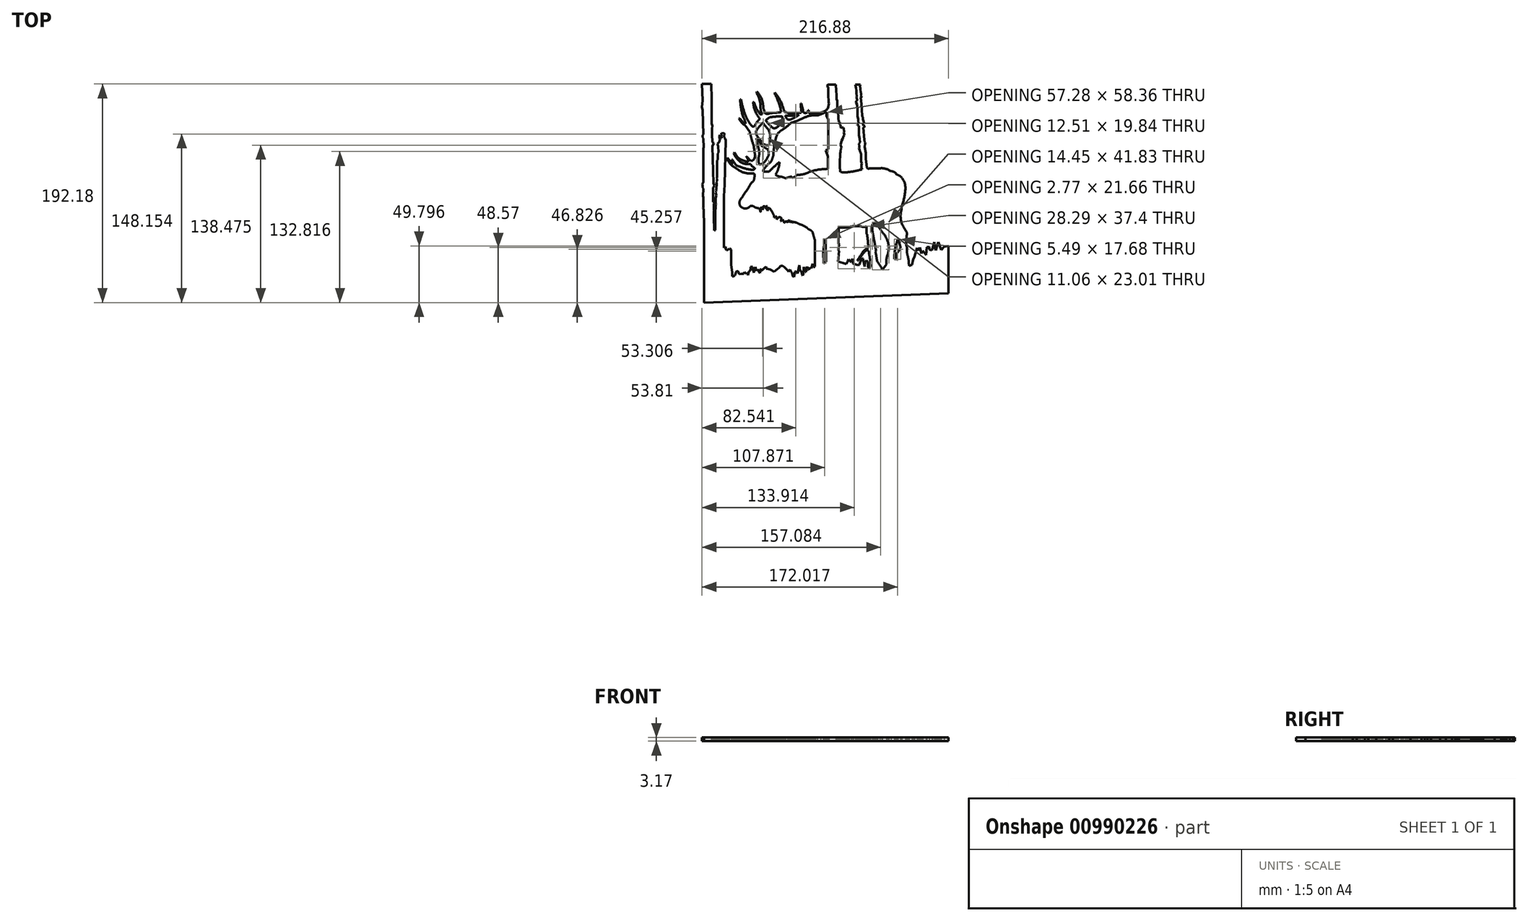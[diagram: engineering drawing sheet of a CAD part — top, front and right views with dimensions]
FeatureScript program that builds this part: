
annotation { "Feature Type Name" : "Feature", "Feature Type Description" : "" }
export const myFeature = defineFeature(function(context is Context, id is Id, definition is map)
    precondition{}
    {
        {
            var Q0;
            Q0=qCreatedBy(makeId("Top.planeOp"),FACE);
            var sketch = newSketch(context, id + "F0", { "sketchPlane" : qUnion([Q0])});
            skArc(sketch, "E0", {"start": v(289.3, 112.58) * mm, "mid": v(291.23, 120.3) * mm, "end": v(292.3, 128.2) * mm});
            skArc(sketch, "E1", {"start": v(292.3, 128.2) * mm, "mid": v(291.34, 133.48) * mm, "end": v(288.53, 138.04) * mm});
            skArc(sketch, "E2", {"start": v(288.53, 138.04) * mm, "mid": v(286.45, 139.47) * mm, "end": v(284.11, 140.41) * mm});
            skArc(sketch, "E3", {"start": v(284.11, 140.41) * mm, "mid": v(282.3, 142.56) * mm, "end": v(279.5, 142.88) * mm});
            skArc(sketch, "E4", {"start": v(279.5, 142.88) * mm, "mid": v(274.89, 145.26) * mm, "end": v(269.71, 145.75) * mm});
            skArc(sketch, "E5", {"start": v(269.71, 145.75) * mm, "mid": v(260.83, 145.51) * mm, "end": v(252.03, 144.24) * mm});
            skArc(sketch, "E6", {"start": v(239.59, 142.06) * mm, "mid": v(245.85, 142.93) * mm, "end": v(252.03, 144.24) * mm});
            skArc(sketch, "E7", {"start": v(231.89, 143.51) * mm, "mid": v(235.66, 142.4) * mm, "end": v(239.59, 142.06) * mm});
            skArc(sketch, "E8", {"start": v(231.89, 143.51) * mm, "mid": v(226.66, 145.01) * mm, "end": v(221.22, 144.97) * mm});
            skArc(sketch, "E9", {"start": v(221.22, 144.97) * mm, "mid": v(212.73, 143.94) * mm, "end": v(204.68, 141.05) * mm});
            skArc(sketch, "E10", {"start": v(196.66, 139.78) * mm, "mid": v(200.7, 140.17) * mm, "end": v(204.68, 141.05) * mm});
            skArc(sketch, "E11", {"start": v(193.06, 137.4) * mm, "mid": v(195.05, 138.3) * mm, "end": v(196.66, 139.78) * mm});
            skArc(sketch, "E12", {"start": v(192.24, 138.4) * mm, "mid": v(192.5, 137.79) * mm, "end": v(193.06, 137.4) * mm});
            skArc(sketch, "E13", {"start": v(192.24, 138.4) * mm, "mid": v(189.53, 137.79) * mm, "end": v(186.88, 136.94) * mm});
            skArc(sketch, "E14", {"start": v(186.88, 136.94) * mm, "mid": v(184.76, 137.84) * mm, "end": v(182.54, 138.4) * mm});
            skArc(sketch, "E15", {"start": v(178.04, 140.2) * mm, "mid": v(180.12, 138.87) * mm, "end": v(182.54, 138.4) * mm});
            skArc(sketch, "E16", {"start": v(178.04, 140.2) * mm, "mid": v(179.67, 143.2) * mm, "end": v(180.75, 146.46) * mm});
            skArc(sketch, "E17", {"start": v(180.75, 146.46) * mm, "mid": v(181.29, 148.76) * mm, "end": v(181.48, 151.1) * mm});
            skArc(sketch, "E18", {"start": v(181.48, 151.1) * mm, "mid": v(176.84, 147.09) * mm, "end": v(172.37, 142.88) * mm});
            skArc(sketch, "E19", {"start": v(172.37, 142.88) * mm, "mid": v(169.86, 142.9) * mm, "end": v(167.36, 142.63) * mm});
            skArc(sketch, "E20", {"start": v(167.36, 144.13) * mm, "mid": v(167.22, 143.38) * mm, "end": v(167.36, 142.63) * mm});
            skArc(sketch, "E21", {"start": v(172.84, 150.42) * mm, "mid": v(169.85, 147.49) * mm, "end": v(167.36, 144.13) * mm});
            skArc(sketch, "E22", {"start": v(172.84, 150.42) * mm, "mid": v(174.3, 152.06) * mm, "end": v(175.16, 154.07) * mm});
            skArc(sketch, "E23", {"start": v(175.16, 154.07) * mm, "mid": v(175.98, 156.69) * mm, "end": v(176.22, 159.42) * mm});
            skArc(sketch, "E24", {"start": v(176.22, 159.42) * mm, "mid": v(176.58, 162.71) * mm, "end": v(176.58, 166.02) * mm});
            skArc(sketch, "E25", {"start": v(179.42, 175.5) * mm, "mid": v(177.9, 170.79) * mm, "end": v(176.58, 166.02) * mm});
            skArc(sketch, "E26", {"start": v(183.87, 179.43) * mm, "mid": v(181.42, 177.71) * mm, "end": v(179.42, 175.5) * mm});
            skArc(sketch, "E27", {"start": v(183.87, 179.43) * mm, "mid": v(187.89, 182.31) * mm, "end": v(191.59, 185.6) * mm});
            skArc(sketch, "E28", {"start": v(191.59, 185.6) * mm, "mid": v(197.29, 187.56) * mm, "end": v(202.79, 190.02) * mm});
            skArc(sketch, "E29", {"start": v(213.12, 192.38) * mm, "mid": v(207.8, 191.86) * mm, "end": v(202.79, 190.02) * mm});
            skArc(sketch, "E30", {"start": v(213.12, 192.38) * mm, "mid": v(215.42, 192.38) * mm, "end": v(217.57, 193.18) * mm});
            skArc(sketch, "E31", {"start": v(217.57, 193.18) * mm, "mid": v(220.8, 194.41) * mm, "end": v(223.92, 195.9) * mm});
            skArc(sketch, "E32", {"start": v(223.92, 195.9) * mm, "mid": v(223.09, 196.45) * mm, "end": v(222.1, 196.3) * mm});
            skArc(sketch, "E33", {"start": v(214.93, 194.33) * mm, "mid": v(218.63, 194.92) * mm, "end": v(222.1, 196.3) * mm});
            skArc(sketch, "E34", {"start": v(209.07, 193.78) * mm, "mid": v(212, 194.03) * mm, "end": v(214.93, 194.33) * mm});
            skArc(sketch, "E35", {"start": v(207.58, 194.33) * mm, "mid": v(208.28, 193.93) * mm, "end": v(209.07, 193.78) * mm});
            skArc(sketch, "E36", {"start": v(207.24, 196.65) * mm, "mid": v(207.27, 195.47) * mm, "end": v(207.58, 194.33) * mm});
            skArc(sketch, "E37", {"start": v(205.66, 194.61) * mm, "mid": v(206.33, 195.56) * mm, "end": v(206.7, 196.65) * mm});
            skArc(sketch, "E38", {"start": v(202.79, 194.61) * mm, "mid": v(204.22, 194.36) * mm, "end": v(205.66, 194.61) * mm});
            skArc(sketch, "E39", {"start": v(202.01, 197.08) * mm, "mid": v(202.26, 195.8) * mm, "end": v(202.79, 194.61) * mm});
            skLineSegment(sketch, "E40", {"start": v(202.01, 197.08) * mm, "end": v(200.49, 202.8) * mm});
            skLineSegment(sketch, "E41", {"start": v(200.49, 202.8) * mm, "end": v(200.22, 202.73) * mm});
            skLineSegment(sketch, "E42", {"start": v(200.22, 202.73) * mm, "end": v(200.49, 194.54) * mm});
            skArc(sketch, "E43", {"start": v(193.33, 189.62) * mm, "mid": v(197.21, 191.64) * mm, "end": v(200.49, 194.54) * mm});
            skArc(sketch, "E44", {"start": v(188.45, 188.76) * mm, "mid": v(190.99, 188.63) * mm, "end": v(193.33, 189.62) * mm});
            skArc(sketch, "E45", {"start": v(186.3, 193.22) * mm, "mid": v(187.09, 190.85) * mm, "end": v(188.45, 188.76) * mm});
            skArc(sketch, "E46", {"start": v(186.3, 193.22) * mm, "mid": v(185.25, 197.3) * mm, "end": v(183.9, 201.29) * mm});
            skArc(sketch, "E47", {"start": v(183.9, 201.29) * mm, "mid": v(181.14, 207.1) * mm, "end": v(177.37, 212.32) * mm});
            skArc(sketch, "E48", {"start": v(183.07, 195.14) * mm, "mid": v(180.76, 203.46) * mm, "end": v(177.37, 211.4) * mm});
            skArc(sketch, "E49", {"start": v(183.9, 186.66) * mm, "mid": v(183.95, 190.94) * mm, "end": v(183.07, 195.14) * mm});
            skArc(sketch, "E50", {"start": v(177.97, 181.1) * mm, "mid": v(181.36, 183.42) * mm, "end": v(183.9, 186.66) * mm});
            skArc(sketch, "E51", {"start": v(175, 181.65) * mm, "mid": v(176.4, 180.96) * mm, "end": v(177.97, 181.1) * mm});
            skArc(sketch, "E52", {"start": v(166.84, 190.72) * mm, "mid": v(170.75, 186.04) * mm, "end": v(175, 181.65) * mm});
            skArc(sketch, "E53", {"start": v(161.16, 198.35) * mm, "mid": v(163.8, 194.38) * mm, "end": v(166.84, 190.72) * mm});
            skArc(sketch, "E54", {"start": v(158.99, 204.03) * mm, "mid": v(160.06, 201.19) * mm, "end": v(161.16, 198.35) * mm});
            skArc(sketch, "E55", {"start": v(158.3, 203.88) * mm, "mid": v(159.92, 196.73) * mm, "end": v(163.4, 190.28) * mm});
            skArc(sketch, "E56", {"start": v(163.4, 190.28) * mm, "mid": v(167.42, 184.97) * mm, "end": v(171.65, 179.83) * mm});
            skArc(sketch, "E57", {"start": v(173.38, 173.07) * mm, "mid": v(172.95, 176.56) * mm, "end": v(171.65, 179.83) * mm});
            skArc(sketch, "E58", {"start": v(172.4, 166.8) * mm, "mid": v(173.1, 169.9) * mm, "end": v(173.38, 173.07) * mm});
            skArc(sketch, "E59", {"start": v(169.11, 166.37) * mm, "mid": v(170.85, 165.89) * mm, "end": v(172.4, 166.8) * mm});
            skArc(sketch, "E60", {"start": v(166.33, 168.16) * mm, "mid": v(167.52, 166.95) * mm, "end": v(169.11, 166.37) * mm});
            skArc(sketch, "E61", {"start": v(166.33, 168.16) * mm, "mid": v(165.47, 169.7) * mm, "end": v(164.25, 170.99) * mm});
            skArc(sketch, "E62", {"start": v(161.16, 175.18) * mm, "mid": v(162.63, 173.03) * mm, "end": v(164.25, 170.99) * mm});
            skArc(sketch, "E63", {"start": v(161.16, 178.97) * mm, "mid": v(160.88, 177.07) * mm, "end": v(161.16, 175.18) * mm});
            skArc(sketch, "E64", {"start": v(166.84, 185.72) * mm, "mid": v(163.84, 182.48) * mm, "end": v(161.16, 178.97) * mm});
            skArc(sketch, "E65", {"start": v(164.25, 189.12) * mm, "mid": v(161.66, 186.2) * mm, "end": v(159.52, 182.94) * mm});
            skArc(sketch, "E66", {"start": v(157.26, 182.66) * mm, "mid": v(158.44, 182.4) * mm, "end": v(159.52, 182.94) * mm});
            skArc(sketch, "E67", {"start": v(153.07, 189.08) * mm, "mid": v(155, 185.77) * mm, "end": v(157.26, 182.66) * mm});
            skArc(sketch, "E68", {"start": v(151, 193.71) * mm, "mid": v(152, 191.38) * mm, "end": v(153.07, 189.08) * mm});
            skArc(sketch, "E69", {"start": v(147.59, 206.44) * mm, "mid": v(149.02, 200) * mm, "end": v(151, 193.71) * mm});
            skArc(sketch, "E70", {"start": v(147.04, 206.44) * mm, "mid": v(147.73, 198.23) * mm, "end": v(149.9, 190.28) * mm});
            skArc(sketch, "E71", {"start": v(151.64, 185.2) * mm, "mid": v(151, 187.82) * mm, "end": v(149.9, 190.28) * mm});
            skArc(sketch, "E72", {"start": v(150.85, 185.2) * mm, "mid": v(151.25, 185.08) * mm, "end": v(151.64, 185.2) * mm});
            skArc(sketch, "E73", {"start": v(146.46, 189.67) * mm, "mid": v(148.46, 187.25) * mm, "end": v(150.85, 185.2) * mm});
            skArc(sketch, "E74", {"start": v(146.06, 189.42) * mm, "mid": v(148.1, 186.08) * mm, "end": v(151.15, 183.65) * mm});
            skArc(sketch, "E75", {"start": v(152.05, 182.27) * mm, "mid": v(151.61, 182.97) * mm, "end": v(151.15, 183.65) * mm});
            skArc(sketch, "E76", {"start": v(155.29, 177.66) * mm, "mid": v(153.75, 180.02) * mm, "end": v(152.05, 182.27) * mm});
            skArc(sketch, "E77", {"start": v(157.02, 170.79) * mm, "mid": v(156.22, 174.24) * mm, "end": v(155.29, 177.66) * mm});
            skArc(sketch, "E78", {"start": v(159.52, 160.12) * mm, "mid": v(158.72, 165.56) * mm, "end": v(157.02, 170.79) * mm});
            skArc(sketch, "E79", {"start": v(159.29, 153.94) * mm, "mid": v(159.9, 157.01) * mm, "end": v(159.52, 160.12) * mm});
            skArc(sketch, "E80", {"start": v(156.55, 152.14) * mm, "mid": v(158.13, 152.72) * mm, "end": v(159.29, 153.94) * mm});
            skArc(sketch, "E81", {"start": v(153.07, 155.64) * mm, "mid": v(154.73, 153.8) * mm, "end": v(156.55, 152.14) * mm});
            skArc(sketch, "E82", {"start": v(154.42, 152.35) * mm, "mid": v(153.37, 154.26) * mm, "end": v(152.25, 156.11) * mm});
            skArc(sketch, "E83", {"start": v(153.07, 151.65) * mm, "mid": v(153.84, 151.81) * mm, "end": v(154.42, 152.35) * mm});
            skArc(sketch, "E84", {"start": v(141.96, 159.64) * mm, "mid": v(146.43, 154.14) * mm, "end": v(153.07, 151.65) * mm});
            skArc(sketch, "E85", {"start": v(141.29, 159.06) * mm, "mid": v(144.26, 153.94) * mm, "end": v(148.97, 150.36) * mm});
            skArc(sketch, "E86", {"start": v(148.97, 150.36) * mm, "mid": v(152.47, 149.42) * mm, "end": v(156.1, 149.39) * mm});
            skArc(sketch, "E87", {"start": v(156.1, 149.39) * mm, "mid": v(157.72, 147.28) * mm, "end": v(160, 145.93) * mm});
            skArc(sketch, "E88", {"start": v(158.4, 144.31) * mm, "mid": v(159.39, 144.94) * mm, "end": v(160, 145.93) * mm});
            skArc(sketch, "E89", {"start": v(148.12, 146.55) * mm, "mid": v(153.17, 145) * mm, "end": v(158.4, 144.31) * mm});
            skArc(sketch, "E90", {"start": v(148.12, 146.55) * mm, "mid": v(146.4, 147.2) * mm, "end": v(144.6, 147.58) * mm});
            skArc(sketch, "E91", {"start": v(140.2, 153.4) * mm, "mid": v(142.03, 150.21) * mm, "end": v(144.6, 147.58) * mm});
            skArc(sketch, "E92", {"start": v(139.58, 153.27) * mm, "mid": v(139.92, 151.55) * mm, "end": v(140.69, 149.97) * mm});
            skArc(sketch, "E93", {"start": v(139.76, 150.36) * mm, "mid": v(140.17, 150.04) * mm, "end": v(140.69, 149.97) * mm});
            skArc(sketch, "E94", {"start": v(135.7, 155.25) * mm, "mid": v(137.53, 152.63) * mm, "end": v(139.76, 150.36) * mm});
            skArc(sketch, "E95", {"start": v(135.5, 154.22) * mm, "mid": v(137.59, 150.22) * mm, "end": v(141, 147.27) * mm});
            skArc(sketch, "E96", {"start": v(141, 147.27) * mm, "mid": v(144.17, 145.11) * mm, "end": v(147.43, 143.1) * mm});
            skArc(sketch, "E97", {"start": v(147.43, 143.1) * mm, "mid": v(152.5, 141.42) * mm, "end": v(157.84, 141.17) * mm});
            skArc(sketch, "E98", {"start": v(159.67, 140.41) * mm, "mid": v(158.87, 141.07) * mm, "end": v(157.84, 141.17) * mm});
            skArc(sketch, "E99", {"start": v(158.7, 134.3) * mm, "mid": v(159.38, 137.33) * mm, "end": v(159.67, 140.41) * mm});
            skArc(sketch, "E100", {"start": v(158.7, 134.3) * mm, "mid": v(156.39, 132.34) * mm, "end": v(154.95, 129.66) * mm});
            skArc(sketch, "E101", {"start": v(150.6, 123.43) * mm, "mid": v(152.87, 126.48) * mm, "end": v(154.95, 129.66) * mm});
            skArc(sketch, "E102", {"start": v(150.6, 123.43) * mm, "mid": v(149.9, 122.39) * mm, "end": v(149.4, 121.22) * mm});
            skArc(sketch, "E103", {"start": v(149.4, 121.22) * mm, "mid": v(147.98, 119.38) * mm, "end": v(146.62, 117.49) * mm});
            skArc(sketch, "E104", {"start": v(146.62, 117.49) * mm, "mid": v(146.32, 115.01) * mm, "end": v(146.85, 112.58) * mm});
            skArc(sketch, "E105", {"start": v(146.85, 112.58) * mm, "mid": v(149.45, 110.75) * mm, "end": v(152.62, 110.54) * mm});
            skArc(sketch, "E106", {"start": v(152.62, 110.54) * mm, "mid": v(154.4, 111.28) * mm, "end": v(155.84, 112.58) * mm});
            skArc(sketch, "E107", {"start": v(158.7, 112.26) * mm, "mid": v(157.3, 112.65) * mm, "end": v(155.84, 112.58) * mm});
            skArc(sketch, "E108", {"start": v(158.7, 112.26) * mm, "mid": v(160.93, 111.06) * mm, "end": v(163.4, 110.54) * mm});
            skArc(sketch, "E109", {"start": v(165.3, 192.45) * mm, "mid": v(165.71, 193.54) * mm, "end": v(165.55, 194.68) * mm});
            skArc(sketch, "E110", {"start": v(164.7, 201.29) * mm, "mid": v(164.88, 197.95) * mm, "end": v(165.55, 194.68) * mm});
            skArc(sketch, "E111", {"start": v(164.7, 201.29) * mm, "mid": v(164.52, 203.46) * mm, "end": v(163.96, 205.57) * mm});
            skArc(sketch, "E112", {"start": v(163.96, 205.57) * mm, "mid": v(162.94, 208.94) * mm, "end": v(161.16, 211.98) * mm});
            skArc(sketch, "E113", {"start": v(166.33, 205.57) * mm, "mid": v(164.38, 209.58) * mm, "end": v(161.64, 213.1) * mm});
            skArc(sketch, "E114", {"start": v(167.3, 198.35) * mm, "mid": v(167, 201.99) * mm, "end": v(166.33, 205.57) * mm});
            skArc(sketch, "E115", {"start": v(168.81, 194.23) * mm, "mid": v(168.12, 196.32) * mm, "end": v(167.3, 198.35) * mm});
            skArc(sketch, "E116", {"start": v(168.81, 194.23) * mm, "mid": v(170.96, 193.47) * mm, "end": v(173.12, 194.23) * mm});
            skArc(sketch, "E117", {"start": v(173.12, 194.23) * mm, "mid": v(178.1, 194.59) * mm, "end": v(183.07, 195.14) * mm});
            skArc(sketch, "E118", {"start": v(173.62, 190.72) * mm, "mid": v(171.28, 189.46) * mm, "end": v(169.32, 187.68) * mm});
            skArc(sketch, "E119", {"start": v(183.9, 191.5) * mm, "mid": v(178.75, 191.21) * mm, "end": v(173.62, 190.72) * mm});
            skArc(sketch, "E120", {"start": v(189.3, 194.23) * mm, "mid": v(187.65, 194.94) * mm, "end": v(185.85, 195.14) * mm});
            skArc(sketch, "E121", {"start": v(193.24, 191.98) * mm, "mid": v(189.96, 191.93) * mm, "end": v(186.67, 191.86) * mm});
            skArc(sketch, "E122", {"start": v(198.82, 192.88) * mm, "mid": v(196, 192.6) * mm, "end": v(193.24, 191.98) * mm});
            skArc(sketch, "E123", {"start": v(192.07, 194.23) * mm, "mid": v(196.28, 194.3) * mm, "end": v(200.49, 194.54) * mm});
            skArc(sketch, "E124", {"start": v(189.3, 194.23) * mm, "mid": v(190.69, 194.22) * mm, "end": v(192.07, 194.23) * mm});
            skLineSegment(sketch, "E125", {"start": v(177.37, 212.32) * mm, "end": v(177.37, 211.4) * mm});
            skLineSegment(sketch, "E126", {"start": v(207.24, 196.65) * mm, "end": v(206.7, 196.65) * mm});
            skLineSegment(sketch, "E127", {"start": v(161.64, 213.1) * mm, "end": v(161.16, 211.98) * mm});
            skLineSegment(sketch, "E128", {"start": v(158.99, 204.03) * mm, "end": v(158.3, 203.88) * mm});
            skLineSegment(sketch, "E129", {"start": v(147.59, 206.44) * mm, "end": v(147.04, 206.44) * mm});
            skLineSegment(sketch, "E130", {"start": v(146.46, 189.67) * mm, "end": v(146.06, 189.42) * mm});
            skLineSegment(sketch, "E131", {"start": v(153.07, 155.64) * mm, "end": v(152.25, 156.11) * mm});
            skLineSegment(sketch, "E132", {"start": v(141.96, 159.64) * mm, "end": v(141.29, 159.06) * mm});
            skLineSegment(sketch, "E133", {"start": v(135.7, 155.25) * mm, "end": v(135.5, 154.22) * mm});
            skLineSegment(sketch, "E134", {"start": v(140.2, 153.4) * mm, "end": v(139.58, 153.27) * mm});
            skArc(sketch, "E135", {"start": v(163.1, 151.48) * mm, "mid": v(163.45, 150.17) * mm, "end": v(164.01, 148.95) * mm});
            skArc(sketch, "E136", {"start": v(163.8, 157.7) * mm, "mid": v(163.13, 154.63) * mm, "end": v(163.1, 151.48) * mm});
            skArc(sketch, "E137", {"start": v(164.01, 148.95) * mm, "mid": v(167.52, 150.55) * mm, "end": v(170.05, 153.46) * mm});
            skArc(sketch, "E138", {"start": v(163.8, 157.7) * mm, "mid": v(163.58, 161.1) * mm, "end": v(162.78, 164.42) * mm});
            skArc(sketch, "E139", {"start": v(162.78, 164.42) * mm, "mid": v(161.97, 168.2) * mm, "end": v(161.1, 171.96) * mm});
            skArc(sketch, "E140", {"start": v(164.01, 168.82) * mm, "mid": v(162.59, 170.42) * mm, "end": v(161.1, 171.96) * mm});
            skArc(sketch, "E141", {"start": v(164.01, 168.82) * mm, "mid": v(164.81, 167.13) * mm, "end": v(165.74, 165.51) * mm});
            skArc(sketch, "E142", {"start": v(165.74, 165.51) * mm, "mid": v(168.06, 164.07) * mm, "end": v(170.53, 162.92) * mm});
            skArc(sketch, "E143", {"start": v(171.85, 157.06) * mm, "mid": v(172.03, 160.18) * mm, "end": v(170.53, 162.92) * mm});
            skArc(sketch, "E144", {"start": v(170.05, 153.46) * mm, "mid": v(171, 155.24) * mm, "end": v(171.85, 157.06) * mm});
            skArc(sketch, "E145", {"start": v(164.77, 107.19) * mm, "mid": v(164.32, 108.96) * mm, "end": v(163.4, 110.54) * mm});
            skArc(sketch, "E146", {"start": v(164.77, 107.19) * mm, "mid": v(165.08, 109) * mm, "end": v(164.77, 110.81) * mm});
            skArc(sketch, "E147", {"start": v(166.69, 109.06) * mm, "mid": v(166.32, 110.13) * mm, "end": v(165.5, 110.92) * mm});
            skArc(sketch, "E148", {"start": v(166.69, 109.06) * mm, "mid": v(166.94, 110.54) * mm, "end": v(167.08, 112.04) * mm});
            skArc(sketch, "E149", {"start": v(169.65, 110.01) * mm, "mid": v(169.18, 111.23) * mm, "end": v(168.37, 112.25) * mm});
            skArc(sketch, "E150", {"start": v(169.65, 110.01) * mm, "mid": v(169.8, 111.4) * mm, "end": v(169.86, 112.8) * mm});
            skArc(sketch, "E151", {"start": v(168.37, 112.25) * mm, "mid": v(167.69, 112.37) * mm, "end": v(167.08, 112.04) * mm});
            skArc(sketch, "E152", {"start": v(165.5, 110.92) * mm, "mid": v(165.1, 111.07) * mm, "end": v(164.77, 110.81) * mm});
            skArc(sketch, "E153", {"start": v(171.02, 108.26) * mm, "mid": v(170.68, 110.59) * mm, "end": v(169.86, 112.8) * mm});
            skArc(sketch, "E154", {"start": v(171.02, 108.26) * mm, "mid": v(171.36, 109.8) * mm, "end": v(171.5, 111.36) * mm});
            skArc(sketch, "E155", {"start": v(175.68, 106) * mm, "mid": v(174, 109) * mm, "end": v(171.5, 111.36) * mm});
            skArc(sketch, "E156", {"start": v(176.85, 102.45) * mm, "mid": v(176.58, 104.33) * mm, "end": v(175.68, 106) * mm});
            skArc(sketch, "E157", {"start": v(176.85, 102.45) * mm, "mid": v(177.5, 103) * mm, "end": v(177.97, 103.71) * mm});
            skArc(sketch, "E158", {"start": v(178.84, 100.9) * mm, "mid": v(179.05, 102.5) * mm, "end": v(177.97, 103.71) * mm});
            skArc(sketch, "E159", {"start": v(178.84, 100.9) * mm, "mid": v(179.74, 101.51) * mm, "end": v(180.3, 102.45) * mm});
            skArc(sketch, "E160", {"start": v(183.26, 102.1) * mm, "mid": v(181.82, 102.64) * mm, "end": v(180.3, 102.45) * mm});
            skArc(sketch, "E161", {"start": v(182.62, 99.29) * mm, "mid": v(183.08, 100.66) * mm, "end": v(183.26, 102.1) * mm});
            skArc(sketch, "E162", {"start": v(182.62, 99.29) * mm, "mid": v(183.58, 99.98) * mm, "end": v(184.32, 100.9) * mm});
            skArc(sketch, "E163", {"start": v(185.5, 98.03) * mm, "mid": v(184.95, 99.48) * mm, "end": v(184.32, 100.9) * mm});
            skArc(sketch, "E164", {"start": v(186.41, 97.77) * mm, "mid": v(185.97, 97.94) * mm, "end": v(185.5, 98.03) * mm});
            skArc(sketch, "E165", {"start": v(186.58, 98.91) * mm, "mid": v(186.38, 98.36) * mm, "end": v(186.41, 97.77) * mm});
            skArc(sketch, "E166", {"start": v(188.73, 98.03) * mm, "mid": v(187.84, 98.92) * mm, "end": v(186.58, 98.91) * mm});
            skArc(sketch, "E167", {"start": v(189.5, 100.1) * mm, "mid": v(189.12, 99.06) * mm, "end": v(188.73, 98.03) * mm});
            skArc(sketch, "E168", {"start": v(190.34, 98.37) * mm, "mid": v(190.15, 99.34) * mm, "end": v(189.5, 100.1) * mm});
            skArc(sketch, "E169", {"start": v(190.34, 98.37) * mm, "mid": v(190.68, 98.93) * mm, "end": v(190.92, 99.54) * mm});
            skArc(sketch, "E170", {"start": v(190.92, 99.54) * mm, "mid": v(191.43, 98.86) * mm, "end": v(192.01, 98.24) * mm});
            skArc(sketch, "E171", {"start": v(192.01, 98.24) * mm, "mid": v(192.1, 98.7) * mm, "end": v(192.2, 99.17) * mm});
            skArc(sketch, "E172", {"start": v(193.28, 97.67) * mm, "mid": v(192.85, 98.5) * mm, "end": v(192.2, 99.17) * mm});
            skArc(sketch, "E173", {"start": v(193.5, 98.6) * mm, "mid": v(193.37, 98.14) * mm, "end": v(193.28, 97.67) * mm});
            skArc(sketch, "E174", {"start": v(199.02, 96.53) * mm, "mid": v(196.37, 97.85) * mm, "end": v(193.5, 98.6) * mm});
            skArc(sketch, "E175", {"start": v(205.66, 93.52) * mm, "mid": v(202.47, 95.32) * mm, "end": v(199.02, 96.53) * mm});
            skArc(sketch, "E176", {"start": v(205.66, 93.52) * mm, "mid": v(206.5, 92.51) * mm, "end": v(207.69, 91.92) * mm});
            skArc(sketch, "E177", {"start": v(210.62, 89.56) * mm, "mid": v(209.31, 90.94) * mm, "end": v(207.69, 91.92) * mm});
            skArc(sketch, "E178", {"start": v(210.62, 89.56) * mm, "mid": v(211.53, 86.24) * mm, "end": v(212.55, 82.94) * mm});
            skArc(sketch, "E179", {"start": v(212.55, 59.26) * mm, "mid": v(212.57, 71.1) * mm, "end": v(212.55, 82.94) * mm});
            skLineSegment(sketch, "E180", {"start": v(220.38, 62.07) * mm, "end": v(220, 72) * mm});
            skLineSegment(sketch, "E181", {"start": v(220, 72) * mm, "end": v(219.8, 72.73) * mm});
            skLineSegment(sketch, "E182", {"start": v(219.8, 72.73) * mm, "end": v(220.24, 73.23) * mm});
            skLineSegment(sketch, "E183", {"start": v(220.24, 73.23) * mm, "end": v(220.51, 81.08) * mm});
            skLineSegment(sketch, "E184", {"start": v(220.51, 81.08) * mm, "end": v(221.78, 83.73) * mm});
            skLineSegment(sketch, "E185", {"start": v(221.78, 83.73) * mm, "end": v(222.29, 83.48) * mm});
            skLineSegment(sketch, "E186", {"start": v(222.29, 83.48) * mm, "end": v(222.29, 81.83) * mm});
            skLineSegment(sketch, "E187", {"start": v(222.29, 81.83) * mm, "end": v(222.58, 63.33) * mm});
            skLineSegment(sketch, "E188", {"start": v(233.09, 63.62) * mm, "end": v(233.9, 72.96) * mm});
            skLineSegment(sketch, "E189", {"start": v(233.9, 72.96) * mm, "end": v(233.15, 73.61) * mm});
            skLineSegment(sketch, "E190", {"start": v(233.15, 73.61) * mm, "end": v(233.47, 77.6) * mm});
            skLineSegment(sketch, "E191", {"start": v(233.47, 77.6) * mm, "end": v(234.52, 78.75) * mm});
            skLineSegment(sketch, "E192", {"start": v(234.52, 78.75) * mm, "end": v(233.4, 79.18) * mm});
            skLineSegment(sketch, "E193", {"start": v(233.4, 79.18) * mm, "end": v(233.68, 91.87) * mm});
            skLineSegment(sketch, "E194", {"start": v(233.68, 91.87) * mm, "end": v(233.68, 93.68) * mm});
            skArc(sketch, "E195", {"start": v(233.68, 93.68) * mm, "mid": v(238.34, 93.43) * mm, "end": v(242.94, 94.19) * mm});
            skArc(sketch, "E196", {"start": v(253.14, 94.7) * mm, "mid": v(248.02, 94.87) * mm, "end": v(242.94, 94.19) * mm});
            skArc(sketch, "E197", {"start": v(253.14, 94.7) * mm, "mid": v(255.51, 94.15) * mm, "end": v(257.88, 94.7) * mm});
            skArc(sketch, "E198", {"start": v(257.88, 88.47) * mm, "mid": v(258.03, 91.58) * mm, "end": v(257.88, 94.7) * mm});
            skArc(sketch, "E199", {"start": v(258.81, 85.53) * mm, "mid": v(258.67, 87.1) * mm, "end": v(257.88, 88.47) * mm});
            skArc(sketch, "E200", {"start": v(259.63, 75.7) * mm, "mid": v(259.38, 80.63) * mm, "end": v(258.81, 85.53) * mm});
            skArc(sketch, "E201", {"start": v(257.88, 94.7) * mm, "mid": v(262.14, 95.88) * mm, "end": v(265.8, 98.35) * mm});
            skArc(sketch, "E202", {"start": v(267.93, 95.65) * mm, "mid": v(267.04, 97.14) * mm, "end": v(265.8, 98.35) * mm});
            skArc(sketch, "E203", {"start": v(267.93, 95.65) * mm, "mid": v(269.58, 92.98) * mm, "end": v(271.26, 90.31) * mm});
            skArc(sketch, "E204", {"start": v(276.25, 82.73) * mm, "mid": v(274.09, 86.74) * mm, "end": v(271.26, 90.31) * mm});
            skArc(sketch, "E205", {"start": v(276.83, 70.39) * mm, "mid": v(277.62, 76.61) * mm, "end": v(276.25, 82.73) * mm});
            skArc(sketch, "E206", {"start": v(276.83, 70.39) * mm, "mid": v(275.64, 65.9) * mm, "end": v(275.5, 61.26) * mm});
            skArc(sketch, "E207", {"start": v(282.86, 72.97) * mm, "mid": v(282.62, 69.53) * mm, "end": v(282.63, 66.08) * mm});
            skArc(sketch, "E208", {"start": v(285.61, 83.3) * mm, "mid": v(284.03, 78.2) * mm, "end": v(282.86, 72.97) * mm});
            skArc(sketch, "E209", {"start": v(288.08, 75.5) * mm, "mid": v(287.08, 79.48) * mm, "end": v(285.61, 83.3) * mm});
            skArc(sketch, "E210", {"start": v(288.08, 75.5) * mm, "mid": v(286.28, 72.95) * mm, "end": v(284.52, 70.39) * mm});
            skArc(sketch, "E211", {"start": v(284.52, 65.62) * mm, "mid": v(284.58, 68) * mm, "end": v(284.52, 70.39) * mm});
            skArc(sketch, "E212", {"start": v(295.49, 59.82) * mm, "mid": v(295.27, 62.6) * mm, "end": v(295.03, 65.4) * mm});
            skArc(sketch, "E213", {"start": v(295.03, 65.4) * mm, "mid": v(294.36, 68.4) * mm, "end": v(293.6, 71.36) * mm});
            skArc(sketch, "E214", {"start": v(293.6, 71.36) * mm, "mid": v(293.72, 74.67) * mm, "end": v(293.08, 77.91) * mm});
            skArc(sketch, "E215", {"start": v(293.6, 87.84) * mm, "mid": v(293.1, 82.89) * mm, "end": v(293.08, 77.91) * mm});
            skArc(sketch, "E216", {"start": v(293.6, 87.84) * mm, "mid": v(293.35, 89.65) * mm, "end": v(292.27, 91.12) * mm});
            skArc(sketch, "E217", {"start": v(288.68, 98) * mm, "mid": v(290.4, 94.53) * mm, "end": v(292.27, 91.12) * mm});
            skArc(sketch, "E218", {"start": v(288.68, 109.29) * mm, "mid": v(288.02, 103.65) * mm, "end": v(288.68, 98) * mm});
            skArc(sketch, "E219", {"start": v(289.3, 112.58) * mm, "mid": v(288.87, 110.96) * mm, "end": v(288.68, 109.29) * mm});
            skArc(sketch, "E220", {"start": v(259.63, 75.7) * mm, "mid": v(255.67, 73.06) * mm, "end": v(252.96, 69.15) * mm});
            skArc(sketch, "E221", {"start": v(252.96, 69.15) * mm, "mid": v(251.43, 66.95) * mm, "end": v(250.09, 64.62) * mm});
            skArc(sketch, "E222", {"start": v(258.7, 74.1) * mm, "mid": v(254.29, 69.78) * mm, "end": v(251, 64.56) * mm});
            skArc(sketch, "E223", {"start": v(260.37, 70.39) * mm, "mid": v(259.94, 72.42) * mm, "end": v(258.7, 74.1) * mm});
            skArc(sketch, "E224", {"start": v(261.34, 58.36) * mm, "mid": v(261.22, 64.4) * mm, "end": v(260.37, 70.39) * mm});
            skArc(sketch, "E225", {"start": v(272.08, 56.52) * mm, "mid": v(269.77, 60.5) * mm, "end": v(267.2, 64.33) * mm});
            skArc(sketch, "E226", {"start": v(267.2, 64.33) * mm, "mid": v(266.68, 68.4) * mm, "end": v(265.8, 72.43) * mm});
            skArc(sketch, "E227", {"start": v(266.48, 72.97) * mm, "mid": v(265.48, 78.54) * mm, "end": v(264.33, 84.08) * mm});
            skLineSegment(sketch, "E228", {"start": v(265.8, 72.43) * mm, "end": v(266.48, 72.97) * mm});
            skLineSegment(sketch, "E229", {"start": v(264.33, 84.08) * mm, "end": v(263.18, 91.09) * mm});
            skLineSegment(sketch, "E230", {"start": v(263.18, 91.09) * mm, "end": v(263.18, 96.42) * mm});
            skLineSegment(sketch, "E231", {"start": v(115.29, 50.82) * mm, "end": v(115.29, 87) * mm});
            skLineSegment(sketch, "E232", {"start": v(115.29, 87) * mm, "end": v(115.29, 88.54) * mm});
            skLineSegment(sketch, "E233", {"start": v(115.29, 88.54) * mm, "end": v(115.29, 94.47) * mm});
            skLineSegment(sketch, "E234", {"start": v(115.29, 94.47) * mm, "end": v(114.76, 109.37) * mm});
            skLineSegment(sketch, "E235", {"start": v(114.76, 109.37) * mm, "end": v(114.3, 110.7) * mm});
            skLineSegment(sketch, "E236", {"start": v(114.3, 110.7) * mm, "end": v(114.67, 111.2) * mm});
            skLineSegment(sketch, "E237", {"start": v(114.67, 111.2) * mm, "end": v(114.67, 120.22) * mm});
            skLineSegment(sketch, "E238", {"start": v(114.67, 120.22) * mm, "end": v(114.08, 121.13) * mm});
            skLineSegment(sketch, "E239", {"start": v(114.08, 121.13) * mm, "end": v(114.67, 127.96) * mm});
            skLineSegment(sketch, "E240", {"start": v(114.67, 127.96) * mm, "end": v(113.94, 128.74) * mm});
            skLineSegment(sketch, "E241", {"start": v(113.94, 128.74) * mm, "end": v(114, 130.29) * mm});
            skLineSegment(sketch, "E242", {"start": v(114, 130.29) * mm, "end": v(113.53, 131.7) * mm});
            skLineSegment(sketch, "E243", {"start": v(113.53, 131.7) * mm, "end": v(114.5, 133.43) * mm});
            skLineSegment(sketch, "E244", {"start": v(114.5, 133.43) * mm, "end": v(114.5, 150.34) * mm});
            skLineSegment(sketch, "E245", {"start": v(114.5, 150.34) * mm, "end": v(114.67, 151.53) * mm});
            skLineSegment(sketch, "E246", {"start": v(114.67, 151.53) * mm, "end": v(114.67, 162.6) * mm});
            skLineSegment(sketch, "E247", {"start": v(114.67, 162.6) * mm, "end": v(114.65, 163.34) * mm});
            skLineSegment(sketch, "E248", {"start": v(114.65, 163.34) * mm, "end": v(114.76, 164.15) * mm});
            skLineSegment(sketch, "E249", {"start": v(114.76, 164.15) * mm, "end": v(114.59, 169.25) * mm});
            skLineSegment(sketch, "E250", {"start": v(114.59, 169.25) * mm, "end": v(114.48, 172.13) * mm});
            skLineSegment(sketch, "E251", {"start": v(114.48, 172.13) * mm, "end": v(113.8, 173.04) * mm});
            skLineSegment(sketch, "E252", {"start": v(113.8, 173.04) * mm, "end": v(113.94, 174.72) * mm});
            skLineSegment(sketch, "E253", {"start": v(113.94, 174.72) * mm, "end": v(114.58, 175.4) * mm});
            skLineSegment(sketch, "E254", {"start": v(114.58, 175.4) * mm, "end": v(114.46, 178.91) * mm});
            skLineSegment(sketch, "E255", {"start": v(114.46, 178.91) * mm, "end": v(113.82, 196.92) * mm});
            skLineSegment(sketch, "E256", {"start": v(113.82, 196.92) * mm, "end": v(113.33, 199.54) * mm});
            skLineSegment(sketch, "E257", {"start": v(113.33, 199.54) * mm, "end": v(113.82, 205.36) * mm});
            skLineSegment(sketch, "E258", {"start": v(113.82, 205.36) * mm, "end": v(113.32, 219.82) * mm});
            skLineSegment(sketch, "E259", {"start": v(113.32, 219.82) * mm, "end": v(121.44, 219.82) * mm});
            skLineSegment(sketch, "E260", {"start": v(121.44, 219.82) * mm, "end": v(121.8, 206.66) * mm});
            skLineSegment(sketch, "E261", {"start": v(121.8, 206.66) * mm, "end": v(121.9, 204.01) * mm});
            skLineSegment(sketch, "E262", {"start": v(121.9, 204.01) * mm, "end": v(121.75, 201.12) * mm});
            skLineSegment(sketch, "E263", {"start": v(121.75, 201.12) * mm, "end": v(121.75, 196.4) * mm});
            skLineSegment(sketch, "E264", {"start": v(121.75, 196.4) * mm, "end": v(121.9, 192.28) * mm});
            skLineSegment(sketch, "E265", {"start": v(121.9, 192.28) * mm, "end": v(121.98, 190.08) * mm});
            skLineSegment(sketch, "E266", {"start": v(121.98, 190.08) * mm, "end": v(121.98, 185.14) * mm});
            skLineSegment(sketch, "E267", {"start": v(121.98, 185.14) * mm, "end": v(122.36, 183.1) * mm});
            skLineSegment(sketch, "E268", {"start": v(122.36, 183.1) * mm, "end": v(122.11, 180.46) * mm});
            skLineSegment(sketch, "E269", {"start": v(122.11, 180.46) * mm, "end": v(122.11, 175.44) * mm});
            skLineSegment(sketch, "E270", {"start": v(122.11, 175.44) * mm, "end": v(122.49, 168.9) * mm});
            skLineSegment(sketch, "E271", {"start": v(122.49, 168.9) * mm, "end": v(123.63, 167.82) * mm});
            skLineSegment(sketch, "E272", {"start": v(123.63, 167.82) * mm, "end": v(122.4, 164.88) * mm});
            skLineSegment(sketch, "E273", {"start": v(122.4, 164.88) * mm, "end": v(123.54, 132.58) * mm});
            skLineSegment(sketch, "E274", {"start": v(123.54, 132.58) * mm, "end": v(124, 131.18) * mm});
            skLineSegment(sketch, "E275", {"start": v(124, 131.18) * mm, "end": v(124.25, 130.32) * mm});
            skLineSegment(sketch, "E276", {"start": v(124.25, 130.32) * mm, "end": v(123.07, 128.97) * mm});
            skLineSegment(sketch, "E277", {"start": v(123.07, 128.97) * mm, "end": v(123.07, 116.13) * mm});
            skLineSegment(sketch, "E278", {"start": v(123.07, 116.13) * mm, "end": v(124.12, 115.73) * mm});
            skLineSegment(sketch, "E279", {"start": v(124.12, 115.73) * mm, "end": v(124.23, 115.18) * mm});
            skLineSegment(sketch, "E280", {"start": v(124.23, 115.18) * mm, "end": v(123.75, 114.58) * mm});
            skLineSegment(sketch, "E281", {"start": v(123.75, 114.58) * mm, "end": v(123.75, 109.32) * mm});
            skLineSegment(sketch, "E282", {"start": v(123.75, 109.32) * mm, "end": v(124.1, 108.62) * mm});
            skLineSegment(sketch, "E283", {"start": v(124.1, 108.62) * mm, "end": v(123.78, 107.45) * mm});
            skLineSegment(sketch, "E284", {"start": v(123.78, 107.45) * mm, "end": v(123.78, 103.25) * mm});
            skLineSegment(sketch, "E285", {"start": v(123.78, 103.25) * mm, "end": v(124.2, 91.18) * mm});
            skLineSegment(sketch, "E286", {"start": v(124.2, 91.18) * mm, "end": v(124.9, 91.45) * mm});
            skLineSegment(sketch, "E287", {"start": v(124.9, 91.45) * mm, "end": v(124.9, 106.08) * mm});
            skLineSegment(sketch, "E288", {"start": v(124.9, 106.08) * mm, "end": v(125.3, 113.1) * mm});
            skLineSegment(sketch, "E289", {"start": v(125.3, 113.1) * mm, "end": v(125.62, 114.33) * mm});
            skLineSegment(sketch, "E290", {"start": v(125.62, 114.33) * mm, "end": v(125.21, 115.24) * mm});
            skLineSegment(sketch, "E291", {"start": v(125.21, 115.24) * mm, "end": v(125.46, 119.61) * mm});
            skPoint(sketch, "E291.endSnap0", {"position": v(125.46, 113.71) * mm});
            skLineSegment(sketch, "E292", {"start": v(125.46, 119.61) * mm, "end": v(125.94, 121.76) * mm});
            skLineSegment(sketch, "E293", {"start": v(125.94, 121.76) * mm, "end": v(125.62, 123.53) * mm});
            skLineSegment(sketch, "E294", {"start": v(125.62, 123.53) * mm, "end": v(125.44, 124.44) * mm});
            skLineSegment(sketch, "E295", {"start": v(125.44, 124.44) * mm, "end": v(125.9, 125.22) * mm});
            skLineSegment(sketch, "E296", {"start": v(125.9, 125.22) * mm, "end": v(125.58, 126.22) * mm});
            skLineSegment(sketch, "E297", {"start": v(125.58, 126.22) * mm, "end": v(125.8, 127.63) * mm});
            skLineSegment(sketch, "E298", {"start": v(125.8, 127.63) * mm, "end": v(126.3, 132.15) * mm});
            skLineSegment(sketch, "E299", {"start": v(126.3, 132.15) * mm, "end": v(125.9, 133.7) * mm});
            skLineSegment(sketch, "E300", {"start": v(125.9, 133.7) * mm, "end": v(126.49, 134.56) * mm});
            skLineSegment(sketch, "E301", {"start": v(126.49, 134.56) * mm, "end": v(126.62, 136.3) * mm});
            skLineSegment(sketch, "E302", {"start": v(126.62, 136.3) * mm, "end": v(126.03, 136.61) * mm});
            skLineSegment(sketch, "E303", {"start": v(126.03, 136.61) * mm, "end": v(126.62, 137.43) * mm});
            skLineSegment(sketch, "E304", {"start": v(126.62, 137.43) * mm, "end": v(126.62, 152.6) * mm});
            skLineSegment(sketch, "E305", {"start": v(126.62, 152.6) * mm, "end": v(127.13, 153.38) * mm});
            skLineSegment(sketch, "E306", {"start": v(127.13, 153.38) * mm, "end": v(127.13, 158.76) * mm});
            skLineSegment(sketch, "E307", {"start": v(127.13, 158.76) * mm, "end": v(127.76, 159.54) * mm});
            skLineSegment(sketch, "E308", {"start": v(127.76, 159.54) * mm, "end": v(127.56, 165.37) * mm});
            skLineSegment(sketch, "E309", {"start": v(127.56, 165.37) * mm, "end": v(127.13, 165.92) * mm});
            skLineSegment(sketch, "E310", {"start": v(127.13, 165.92) * mm, "end": v(127.08, 167.1) * mm});
            skLineSegment(sketch, "E311", {"start": v(127.08, 167.1) * mm, "end": v(128.54, 168.88) * mm});
            skLineSegment(sketch, "E312", {"start": v(128.54, 168.88) * mm, "end": v(129.17, 171.3) * mm});
            skLineSegment(sketch, "E313", {"start": v(129.17, 171.3) * mm, "end": v(128.36, 173.25) * mm});
            skLineSegment(sketch, "E314", {"start": v(128.36, 173.25) * mm, "end": v(128.72, 174.67) * mm});
            skLineSegment(sketch, "E315", {"start": v(128.72, 174.67) * mm, "end": v(129.18, 174.98) * mm});
            skLineSegment(sketch, "E316", {"start": v(129.18, 174.98) * mm, "end": v(129.27, 173.7) * mm});
            skLineSegment(sketch, "E317", {"start": v(129.27, 173.7) * mm, "end": v(129.77, 172.43) * mm});
            skLineSegment(sketch, "E318", {"start": v(129.77, 172.43) * mm, "end": v(130.27, 172.39) * mm});
            skLineSegment(sketch, "E319", {"start": v(130.27, 172.39) * mm, "end": v(130.73, 172.93) * mm});
            skLineSegment(sketch, "E320", {"start": v(130.73, 172.93) * mm, "end": v(130.9, 173.75) * mm});
            skLineSegment(sketch, "E321", {"start": v(130.9, 173.75) * mm, "end": v(130.54, 174.2) * mm});
            skLineSegment(sketch, "E322", {"start": v(130.54, 174.2) * mm, "end": v(130.45, 176.9) * mm});
            skLineSegment(sketch, "E323", {"start": v(130.45, 176.9) * mm, "end": v(131.32, 176.35) * mm});
            skLineSegment(sketch, "E324", {"start": v(131.32, 176.35) * mm, "end": v(131.77, 177.17) * mm});
            skLineSegment(sketch, "E325", {"start": v(131.77, 177.17) * mm, "end": v(133.55, 175.71) * mm});
            skLineSegment(sketch, "E326", {"start": v(133.55, 175.71) * mm, "end": v(132.78, 174.76) * mm});
            skLineSegment(sketch, "E327", {"start": v(132.78, 174.76) * mm, "end": v(132.96, 172.89) * mm});
            skLineSegment(sketch, "E328", {"start": v(132.96, 172.89) * mm, "end": v(133.55, 171.89) * mm});
            skLineSegment(sketch, "E329", {"start": v(133.55, 171.89) * mm, "end": v(134.19, 170.52) * mm});
            skLineSegment(sketch, "E330", {"start": v(134.19, 170.52) * mm, "end": v(133.23, 131.37) * mm});
            skLineSegment(sketch, "E331", {"start": v(133.23, 131.37) * mm, "end": v(132.78, 121.2) * mm});
            skLineSegment(sketch, "E332", {"start": v(132.78, 121.2) * mm, "end": v(132.78, 107.22) * mm});
            skLineSegment(sketch, "E333", {"start": v(132.78, 107.22) * mm, "end": v(132.78, 90.36) * mm});
            skLineSegment(sketch, "E334", {"start": v(132.78, 90.36) * mm, "end": v(132.78, 75.73) * mm});
            skLineSegment(sketch, "E335", {"start": v(132.78, 75.73) * mm, "end": v(134.1, 76.78) * mm});
            skLineSegment(sketch, "E336", {"start": v(134.1, 76.78) * mm, "end": v(134.1, 74.77) * mm});
            skLineSegment(sketch, "E337", {"start": v(134.1, 74.77) * mm, "end": v(134.92, 73.54) * mm});
            skLineSegment(sketch, "E338", {"start": v(134.92, 73.54) * mm, "end": v(136.24, 74.13) * mm});
            skLineSegment(sketch, "E339", {"start": v(136.24, 74.13) * mm, "end": v(137.52, 75.27) * mm});
            skLineSegment(sketch, "E340", {"start": v(137.52, 75.27) * mm, "end": v(139.11, 74.09) * mm});
            skLineSegment(sketch, "E341", {"start": v(139.11, 74.09) * mm, "end": v(139.11, 60.83) * mm});
            skLineSegment(sketch, "E342", {"start": v(139.11, 60.83) * mm, "end": v(139.98, 54.3) * mm});
            skLineSegment(sketch, "E343", {"start": v(139.98, 54.3) * mm, "end": v(139.98, 50.62) * mm});
            skLineSegment(sketch, "E344", {"start": v(224.04, 145.19) * mm, "end": v(224.04, 156.28) * mm});
            skLineSegment(sketch, "E345", {"start": v(224.04, 156.28) * mm, "end": v(222.32, 161.56) * mm});
            skLineSegment(sketch, "E346", {"start": v(222.32, 161.56) * mm, "end": v(224.5, 162.48) * mm});
            skLineSegment(sketch, "E347", {"start": v(224.5, 162.48) * mm, "end": v(224.5, 181.43) * mm});
            skLineSegment(sketch, "E348", {"start": v(224.5, 181.43) * mm, "end": v(224.5, 188.49) * mm});
            skLineSegment(sketch, "E349", {"start": v(224.5, 188.49) * mm, "end": v(222.84, 191.88) * mm});
            skLineSegment(sketch, "E350", {"start": v(222.84, 191.88) * mm, "end": v(222.78, 195.08) * mm});
            skLineSegment(sketch, "E351", {"start": v(222.78, 195.08) * mm, "end": v(222.72, 195.3) * mm});
            skLineSegment(sketch, "E352", {"start": v(222.79, 196.48) * mm, "end": v(223.2, 197.8) * mm});
            skLineSegment(sketch, "E353", {"start": v(223.2, 197.8) * mm, "end": v(224.2, 198.5) * mm});
            skLineSegment(sketch, "E354", {"start": v(224.2, 198.5) * mm, "end": v(224.95, 202.87) * mm});
            skLineSegment(sketch, "E355", {"start": v(224.95, 202.87) * mm, "end": v(224.64, 203.7) * mm});
            skLineSegment(sketch, "E356", {"start": v(224.64, 203.7) * mm, "end": v(224.3, 210.85) * mm});
            skLineSegment(sketch, "E357", {"start": v(224.3, 210.85) * mm, "end": v(224.3, 212.87) * mm});
            skLineSegment(sketch, "E358", {"start": v(224.3, 212.87) * mm, "end": v(224.3, 217.14) * mm});
            skLineSegment(sketch, "E359", {"start": v(224.3, 217.14) * mm, "end": v(223.26, 217.94) * mm});
            skLineSegment(sketch, "E360", {"start": v(223.26, 217.94) * mm, "end": v(224.22, 219.21) * mm});
            skLineSegment(sketch, "E361", {"start": v(224.22, 219.21) * mm, "end": v(231.14, 219.21) * mm});
            skLineSegment(sketch, "E362", {"start": v(231.14, 219.21) * mm, "end": v(231.43, 214) * mm});
            skLineSegment(sketch, "E363", {"start": v(231.43, 214) * mm, "end": v(231.83, 210.23) * mm});
            skLineSegment(sketch, "E364", {"start": v(231.83, 210.23) * mm, "end": v(231.83, 206.47) * mm});
            skLineSegment(sketch, "E365", {"start": v(231.83, 206.47) * mm, "end": v(232.42, 204.92) * mm});
            skLineSegment(sketch, "E366", {"start": v(232.42, 204.92) * mm, "end": v(232.26, 203.54) * mm});
            skLineSegment(sketch, "E367", {"start": v(232.26, 203.54) * mm, "end": v(232.26, 200.61) * mm});
            skLineSegment(sketch, "E368", {"start": v(232.26, 200.61) * mm, "end": v(232.55, 197.8) * mm});
            skLineSegment(sketch, "E369", {"start": v(232.55, 197.8) * mm, "end": v(233.6, 197.14) * mm});
            skLineSegment(sketch, "E370", {"start": v(233.6, 197.14) * mm, "end": v(232.86, 195.95) * mm});
            skLineSegment(sketch, "E371", {"start": v(232.86, 195.95) * mm, "end": v(233.38, 190.2) * mm});
            skLineSegment(sketch, "E372", {"start": v(233.38, 190.2) * mm, "end": v(233.64, 186.47) * mm});
            skLineSegment(sketch, "E373", {"start": v(233.64, 186.47) * mm, "end": v(234.54, 186.22) * mm});
            skLineSegment(sketch, "E374", {"start": v(234.54, 186.22) * mm, "end": v(234.47, 185.24) * mm});
            skLineSegment(sketch, "E375", {"start": v(234.47, 185.24) * mm, "end": v(234.25, 184.12) * mm});
            skLineSegment(sketch, "E376", {"start": v(234.25, 184.12) * mm, "end": v(235.3, 183.91) * mm});
            skLineSegment(sketch, "E377", {"start": v(235.3, 183.91) * mm, "end": v(235.27, 182.85) * mm});
            skLineSegment(sketch, "E378", {"start": v(235.27, 182.85) * mm, "end": v(234.98, 182.2) * mm});
            skLineSegment(sketch, "E379", {"start": v(234.98, 182.2) * mm, "end": v(235.6, 181.66) * mm});
            skLineSegment(sketch, "E380", {"start": v(235.6, 181.66) * mm, "end": v(236.9, 181.59) * mm});
            skLineSegment(sketch, "E381", {"start": v(236.9, 181.59) * mm, "end": v(237.65, 181.44) * mm});
            skLineSegment(sketch, "E382", {"start": v(237.65, 181.44) * mm, "end": v(238.05, 180.1) * mm});
            skLineSegment(sketch, "E383", {"start": v(238.05, 180.1) * mm, "end": v(238.3, 178.15) * mm});
            skLineSegment(sketch, "E384", {"start": v(238.3, 178.15) * mm, "end": v(237.94, 177.43) * mm});
            skLineSegment(sketch, "E385", {"start": v(237.94, 177.43) * mm, "end": v(238.23, 175.76) * mm});
            skLineSegment(sketch, "E386", {"start": v(238.23, 175.76) * mm, "end": v(238.6, 174.79) * mm});
            skLineSegment(sketch, "E387", {"start": v(238.6, 174.79) * mm, "end": v(237.65, 173.92) * mm});
            skLineSegment(sketch, "E388", {"start": v(237.65, 173.92) * mm, "end": v(237.3, 172.62) * mm});
            skLineSegment(sketch, "E389", {"start": v(237.3, 172.62) * mm, "end": v(237.22, 171.68) * mm});
            skLineSegment(sketch, "E390", {"start": v(237.22, 171.68) * mm, "end": v(236.17, 170.01) * mm});
            skLineSegment(sketch, "E391", {"start": v(236.17, 170.01) * mm, "end": v(235.9, 168.6) * mm});
            skLineSegment(sketch, "E392", {"start": v(235.9, 168.6) * mm, "end": v(235.6, 167.52) * mm});
            skLineSegment(sketch, "E393", {"start": v(235.6, 167.52) * mm, "end": v(235.3, 166.73) * mm});
            skLineSegment(sketch, "E394", {"start": v(235.3, 166.73) * mm, "end": v(235.46, 165.46) * mm});
            skLineSegment(sketch, "E395", {"start": v(235.46, 165.46) * mm, "end": v(235.83, 164.7) * mm});
            skLineSegment(sketch, "E396", {"start": v(235.83, 164.7) * mm, "end": v(235.99, 163.86) * mm});
            skLineSegment(sketch, "E397", {"start": v(235.99, 163.86) * mm, "end": v(235.66, 163.12) * mm});
            skLineSegment(sketch, "E398", {"start": v(235.66, 163.12) * mm, "end": v(235.37, 162.68) * mm});
            skLineSegment(sketch, "E399", {"start": v(235.37, 162.68) * mm, "end": v(235.3, 160.76) * mm});
            skLineSegment(sketch, "E400", {"start": v(235.3, 160.76) * mm, "end": v(235.12, 159.91) * mm});
            skLineSegment(sketch, "E401", {"start": v(235.12, 159.91) * mm, "end": v(234.83, 158.9) * mm});
            skLineSegment(sketch, "E402", {"start": v(234.83, 158.9) * mm, "end": v(234.83, 156.26) * mm});
            skLineSegment(sketch, "E403", {"start": v(234.83, 156.26) * mm, "end": v(234.65, 152.99) * mm});
            skLineSegment(sketch, "E404", {"start": v(234.65, 152.99) * mm, "end": v(234.65, 150.06) * mm});
            skLineSegment(sketch, "E405", {"start": v(234.65, 150.06) * mm, "end": v(234.67, 148.2) * mm});
            skLineSegment(sketch, "E406", {"start": v(234.67, 148.2) * mm, "end": v(234.68, 146.84) * mm});
            skLineSegment(sketch, "E407", {"start": v(234.68, 146.84) * mm, "end": v(234.98, 143.58) * mm});
            skLineSegment(sketch, "E408", {"start": v(234.98, 143.58) * mm, "end": v(235.27, 142.48) * mm});
            skLineSegment(sketch, "E409", {"start": v(259.18, 145.35) * mm, "end": v(258.24, 146.21) * mm});
            skLineSegment(sketch, "E410", {"start": v(258.24, 146.21) * mm, "end": v(257.45, 154.28) * mm});
            skLineSegment(sketch, "E411", {"start": v(257.45, 154.28) * mm, "end": v(257.45, 159.27) * mm});
            skLineSegment(sketch, "E412", {"start": v(257.45, 159.27) * mm, "end": v(256.58, 164.51) * mm});
            skLineSegment(sketch, "E413", {"start": v(256.58, 164.51) * mm, "end": v(256.65, 167.62) * mm});
            skLineSegment(sketch, "E414", {"start": v(256.65, 167.62) * mm, "end": v(257.23, 168.35) * mm});
            skLineSegment(sketch, "E415", {"start": v(257.23, 168.35) * mm, "end": v(256.58, 168.96) * mm});
            skLineSegment(sketch, "E416", {"start": v(256.58, 168.96) * mm, "end": v(256.14, 170.73) * mm});
            skLineSegment(sketch, "E417", {"start": v(256.14, 170.73) * mm, "end": v(255.2, 181.55) * mm});
            skLineSegment(sketch, "E418", {"start": v(255.2, 181.55) * mm, "end": v(256.29, 182.1) * mm});
            skLineSegment(sketch, "E419", {"start": v(256.29, 182.1) * mm, "end": v(256.8, 183.14) * mm});
            skLineSegment(sketch, "E420", {"start": v(256.8, 183.14) * mm, "end": v(255.13, 183.14) * mm});
            skLineSegment(sketch, "E421", {"start": v(255.13, 183.14) * mm, "end": v(254.8, 184.95) * mm});
            skLineSegment(sketch, "E422", {"start": v(254.8, 184.95) * mm, "end": v(255.67, 185.67) * mm});
            skLineSegment(sketch, "E423", {"start": v(255.67, 185.67) * mm, "end": v(255.56, 187.05) * mm});
            skLineSegment(sketch, "E424", {"start": v(255.56, 187.05) * mm, "end": v(254.88, 188.68) * mm});
            skLineSegment(sketch, "E425", {"start": v(254.88, 188.68) * mm, "end": v(254.99, 190.77) * mm});
            skLineSegment(sketch, "E426", {"start": v(254.99, 190.77) * mm, "end": v(254.48, 191.14) * mm});
            skLineSegment(sketch, "E427", {"start": v(254.48, 191.14) * mm, "end": v(254.3, 192.11) * mm});
            skLineSegment(sketch, "E428", {"start": v(254.3, 192.11) * mm, "end": v(253.65, 202.17) * mm});
            skLineSegment(sketch, "E429", {"start": v(253.65, 202.17) * mm, "end": v(253.1, 207.77) * mm});
            skLineSegment(sketch, "E430", {"start": v(253.1, 207.77) * mm, "end": v(253.95, 209.4) * mm});
            skLineSegment(sketch, "E431", {"start": v(253.95, 209.4) * mm, "end": v(253.21, 209.9) * mm});
            skLineSegment(sketch, "E432", {"start": v(253.21, 209.9) * mm, "end": v(253.21, 211.86) * mm});
            skLineSegment(sketch, "E433", {"start": v(253.21, 211.86) * mm, "end": v(252.96, 212.48) * mm});
            skLineSegment(sketch, "E434", {"start": v(252.96, 212.48) * mm, "end": v(252.53, 215.59) * mm});
            skLineSegment(sketch, "E435", {"start": v(252.53, 215.59) * mm, "end": v(252.38, 218.23) * mm});
            skLineSegment(sketch, "E436", {"start": v(252.38, 218.23) * mm, "end": v(252.49, 219.46) * mm});
            skLineSegment(sketch, "E437", {"start": v(252.49, 219.46) * mm, "end": v(248.33, 219.46) * mm});
            skLineSegment(sketch, "E438", {"start": v(248.33, 219.46) * mm, "end": v(248.7, 216.2) * mm});
            skLineSegment(sketch, "E439", {"start": v(248.7, 216.2) * mm, "end": v(249.13, 214.32) * mm});
            skLineSegment(sketch, "E440", {"start": v(249.13, 214.32) * mm, "end": v(249.16, 211.75) * mm});
            skLineSegment(sketch, "E441", {"start": v(249.16, 211.75) * mm, "end": v(249.38, 209.26) * mm});
            skLineSegment(sketch, "E442", {"start": v(249.38, 209.26) * mm, "end": v(249.27, 208.39) * mm});
            skLineSegment(sketch, "E443", {"start": v(249.27, 208.39) * mm, "end": v(249.7, 206.04) * mm});
            skLineSegment(sketch, "E444", {"start": v(249.7, 206.04) * mm, "end": v(249.67, 205.24) * mm});
            skLineSegment(sketch, "E445", {"start": v(249.67, 205.24) * mm, "end": v(248.87, 204.74) * mm});
            skLineSegment(sketch, "E446", {"start": v(248.87, 204.74) * mm, "end": v(248.87, 203.47) * mm});
            skLineSegment(sketch, "E447", {"start": v(248.87, 203.47) * mm, "end": v(249.78, 201.95) * mm});
            skLineSegment(sketch, "E448", {"start": v(249.78, 201.95) * mm, "end": v(250.07, 197.83) * mm});
            skLineSegment(sketch, "E449", {"start": v(250.07, 197.83) * mm, "end": v(250.17, 195.26) * mm});
            skLineSegment(sketch, "E450", {"start": v(250.17, 195.26) * mm, "end": v(250.17, 191.2) * mm});
            skLineSegment(sketch, "E451", {"start": v(250.17, 191.2) * mm, "end": v(250.65, 189.3) * mm});
            skLineSegment(sketch, "E452", {"start": v(250.65, 189.3) * mm, "end": v(250.86, 187.77) * mm});
            skLineSegment(sketch, "E453", {"start": v(250.86, 187.77) * mm, "end": v(251.15, 184.91) * mm});
            skLineSegment(sketch, "E454", {"start": v(251.15, 184.91) * mm, "end": v(249.81, 184.52) * mm});
            skLineSegment(sketch, "E455", {"start": v(249.81, 184.52) * mm, "end": v(250.02, 183.83) * mm});
            skLineSegment(sketch, "E456", {"start": v(250.02, 183.83) * mm, "end": v(251.33, 183.04) * mm});
            skLineSegment(sketch, "E457", {"start": v(251.33, 183.04) * mm, "end": v(251.5, 181.86) * mm});
            skLineSegment(sketch, "E458", {"start": v(251.5, 181.86) * mm, "end": v(251.5, 174.8) * mm});
            skLineSegment(sketch, "E459", {"start": v(251.5, 174.8) * mm, "end": v(251.94, 171.6) * mm});
            skLineSegment(sketch, "E460", {"start": v(251.94, 171.6) * mm, "end": v(252.22, 168.47) * mm});
            skLineSegment(sketch, "E461", {"start": v(252.22, 168.47) * mm, "end": v(251.4, 167.14) * mm});
            skLineSegment(sketch, "E462", {"start": v(251.4, 167.14) * mm, "end": v(251.72, 165.46) * mm});
            skLineSegment(sketch, "E463", {"start": v(251.72, 165.46) * mm, "end": v(251.72, 164.18) * mm});
            skLineSegment(sketch, "E464", {"start": v(251.72, 164.18) * mm, "end": v(251.49, 163.27) * mm});
            skLineSegment(sketch, "E465", {"start": v(251.49, 163.27) * mm, "end": v(251.94, 162) * mm});
            skLineSegment(sketch, "E466", {"start": v(251.94, 162) * mm, "end": v(252.45, 160.49) * mm});
            skLineSegment(sketch, "E467", {"start": v(252.45, 160.49) * mm, "end": v(252.81, 159.26) * mm});
            skLineSegment(sketch, "E468", {"start": v(252.81, 159.26) * mm, "end": v(253.36, 158.12) * mm});
            skLineSegment(sketch, "E469", {"start": v(253.36, 158.12) * mm, "end": v(253.4, 153.6) * mm});
            skLineSegment(sketch, "E470", {"start": v(253.4, 153.6) * mm, "end": v(253.27, 151.74) * mm});
            skLineSegment(sketch, "E471", {"start": v(253.27, 151.74) * mm, "end": v(253.81, 150.1) * mm});
            skLineSegment(sketch, "E472", {"start": v(253.81, 150.1) * mm, "end": v(253.68, 148.41) * mm});
            skLineSegment(sketch, "E473", {"start": v(253.68, 148.41) * mm, "end": v(253.59, 146.27) * mm});
            skLineSegment(sketch, "E474", {"start": v(253.59, 146.27) * mm, "end": v(254.28, 144.67) * mm});
            skLineSegment(sketch, "E475", {"start": v(212.55, 59.26) * mm, "end": v(211.34, 58.65) * mm});
            skLineSegment(sketch, "E476", {"start": v(211.34, 58.65) * mm, "end": v(210.75, 61.84) * mm});
            skLineSegment(sketch, "E477", {"start": v(210.75, 61.84) * mm, "end": v(209.34, 57.65) * mm});
            skLineSegment(sketch, "E478", {"start": v(209.34, 57.65) * mm, "end": v(208.33, 58.65) * mm});
            skLineSegment(sketch, "E479", {"start": v(208.33, 58.65) * mm, "end": v(207.24, 56.37) * mm});
            skLineSegment(sketch, "E480", {"start": v(207.24, 56.37) * mm, "end": v(206.7, 56.64) * mm});
            skLineSegment(sketch, "E481", {"start": v(206.7, 56.64) * mm, "end": v(205.78, 59.26) * mm});
            skLineSegment(sketch, "E482", {"start": v(205.78, 59.26) * mm, "end": v(204.64, 54.55) * mm});
            skLineSegment(sketch, "E483", {"start": v(204.64, 54.55) * mm, "end": v(204.05, 54.5) * mm});
            skLineSegment(sketch, "E484", {"start": v(204.05, 54.5) * mm, "end": v(202.91, 59.06) * mm});
            skLineSegment(sketch, "E485", {"start": v(202.91, 59.06) * mm, "end": v(202.36, 52.73) * mm});
            skLineSegment(sketch, "E486", {"start": v(202.36, 52.73) * mm, "end": v(202, 51.4) * mm});
            skLineSegment(sketch, "E487", {"start": v(202, 51.4) * mm, "end": v(201.27, 52.45) * mm});
            skLineSegment(sketch, "E488", {"start": v(201.27, 52.45) * mm, "end": v(200.9, 54.91) * mm});
            skLineSegment(sketch, "E489", {"start": v(200.9, 54.91) * mm, "end": v(199.77, 55.69) * mm});
            skLineSegment(sketch, "E490", {"start": v(199.77, 55.69) * mm, "end": v(199, 60.65) * mm});
            skLineSegment(sketch, "E491", {"start": v(199, 60.65) * mm, "end": v(197.49, 53.32) * mm});
            skLineSegment(sketch, "E492", {"start": v(197.49, 53.32) * mm, "end": v(195.98, 55.28) * mm});
            skLineSegment(sketch, "E493", {"start": v(195.98, 55.28) * mm, "end": v(195.2, 54.87) * mm});
            skLineSegment(sketch, "E494", {"start": v(195.2, 54.87) * mm, "end": v(194.07, 50.17) * mm});
            skLineSegment(sketch, "E495", {"start": v(194.07, 50.17) * mm, "end": v(193.16, 50.86) * mm});
            skLineSegment(sketch, "E496", {"start": v(193.16, 50.86) * mm, "end": v(192.66, 53.5) * mm});
            skLineSegment(sketch, "E497", {"start": v(192.66, 53.5) * mm, "end": v(191.75, 54.96) * mm});
            skLineSegment(sketch, "E498", {"start": v(191.75, 54.96) * mm, "end": v(190.74, 56.64) * mm});
            skLineSegment(sketch, "E499", {"start": v(190.74, 56.64) * mm, "end": v(189.47, 54.96) * mm});
            skLineSegment(sketch, "E500", {"start": v(189.47, 54.96) * mm, "end": v(188.42, 56.23) * mm});
            skLineSegment(sketch, "E501", {"start": v(188.42, 56.23) * mm, "end": v(186.1, 58.6) * mm});
            skLineSegment(sketch, "E502", {"start": v(186.1, 58.6) * mm, "end": v(184.32, 59.88) * mm});
            skLineSegment(sketch, "E503", {"start": v(184.32, 59.88) * mm, "end": v(182.59, 59.97) * mm});
            skLineSegment(sketch, "E504", {"start": v(182.59, 59.97) * mm, "end": v(181.13, 58.38) * mm});
            skLineSegment(sketch, "E505", {"start": v(181.13, 58.38) * mm, "end": v(179.62, 57) * mm});
            skLineSegment(sketch, "E506", {"start": v(179.62, 57) * mm, "end": v(176.66, 54.82) * mm});
            skLineSegment(sketch, "E507", {"start": v(176.66, 54.82) * mm, "end": v(173.43, 56.6) * mm});
            skLineSegment(sketch, "E508", {"start": v(173.43, 56.6) * mm, "end": v(170.83, 57.28) * mm});
            skLineSegment(sketch, "E509", {"start": v(170.83, 57.28) * mm, "end": v(169.73, 57.51) * mm});
            skLineSegment(sketch, "E510", {"start": v(169.73, 57.51) * mm, "end": v(169.73, 59.26) * mm});
            skLineSegment(sketch, "E511", {"start": v(169.73, 59.26) * mm, "end": v(168.37, 58.47) * mm});
            skLineSegment(sketch, "E512", {"start": v(168.37, 58.47) * mm, "end": v(167.1, 57) * mm});
            skLineSegment(sketch, "E513", {"start": v(167.1, 57) * mm, "end": v(166, 55.92) * mm});
            skLineSegment(sketch, "E514", {"start": v(166, 55.92) * mm, "end": v(165.77, 55.87) * mm});
            skLineSegment(sketch, "E515", {"start": v(165.77, 55.87) * mm, "end": v(165.4, 57.46) * mm});
            skLineSegment(sketch, "E516", {"start": v(165.4, 57.46) * mm, "end": v(164.45, 55.96) * mm});
            skLineSegment(sketch, "E517", {"start": v(164.45, 55.96) * mm, "end": v(164.31, 53.68) * mm});
            skLineSegment(sketch, "E518", {"start": v(164.31, 53.68) * mm, "end": v(163.35, 54.6) * mm});
            skLineSegment(sketch, "E519", {"start": v(163.35, 54.6) * mm, "end": v(162.44, 57.1) * mm});
            skLineSegment(sketch, "E520", {"start": v(162.44, 57.1) * mm, "end": v(161.58, 55.32) * mm});
            skLineSegment(sketch, "E521", {"start": v(161.58, 55.32) * mm, "end": v(160.76, 56.7) * mm});
            skLineSegment(sketch, "E522", {"start": v(160.76, 56.7) * mm, "end": v(160.12, 58.88) * mm});
            skLineSegment(sketch, "E523", {"start": v(160.12, 58.88) * mm, "end": v(159.39, 56.19) * mm});
            skLineSegment(sketch, "E524", {"start": v(159.39, 56.19) * mm, "end": v(158.89, 53.86) * mm});
            skLineSegment(sketch, "E525", {"start": v(158.89, 53.86) * mm, "end": v(158.52, 55.14) * mm});
            skLineSegment(sketch, "E526", {"start": v(158.52, 55.14) * mm, "end": v(158.07, 56.55) * mm});
            skLineSegment(sketch, "E527", {"start": v(158.07, 56.55) * mm, "end": v(157.66, 58.83) * mm});
            skLineSegment(sketch, "E528", {"start": v(157.66, 58.83) * mm, "end": v(157.16, 59.33) * mm});
            skLineSegment(sketch, "E529", {"start": v(157.16, 59.33) * mm, "end": v(156.06, 58.92) * mm});
            skLineSegment(sketch, "E530", {"start": v(156.06, 58.92) * mm, "end": v(156.1, 57.2) * mm});
            skLineSegment(sketch, "E531", {"start": v(156.1, 57.2) * mm, "end": v(155.47, 55.5) * mm});
            skLineSegment(sketch, "E532", {"start": v(155.47, 55.5) * mm, "end": v(154.51, 54.96) * mm});
            skLineSegment(sketch, "E533", {"start": v(154.51, 54.96) * mm, "end": v(154.28, 53.55) * mm});
            skLineSegment(sketch, "E534", {"start": v(154.28, 53.55) * mm, "end": v(154.01, 51.54) * mm});
            skLineSegment(sketch, "E535", {"start": v(154.01, 51.54) * mm, "end": v(153.15, 52.9) * mm});
            skLineSegment(sketch, "E536", {"start": v(153.15, 52.9) * mm, "end": v(152.46, 54) * mm});
            skLineSegment(sketch, "E537", {"start": v(152.46, 54) * mm, "end": v(151.87, 53.04) * mm});
            skLineSegment(sketch, "E538", {"start": v(151.87, 53.04) * mm, "end": v(150.87, 54.37) * mm});
            skLineSegment(sketch, "E539", {"start": v(150.87, 54.37) * mm, "end": v(150, 52.9) * mm});
            skLineSegment(sketch, "E540", {"start": v(150, 52.9) * mm, "end": v(147.81, 52.86) * mm});
            skLineSegment(sketch, "E541", {"start": v(147.81, 52.86) * mm, "end": v(145.9, 52.59) * mm});
            skLineSegment(sketch, "E542", {"start": v(145.9, 52.59) * mm, "end": v(145.63, 54.27) * mm});
            skLineSegment(sketch, "E543", {"start": v(145.63, 54.27) * mm, "end": v(145.03, 55.28) * mm});
            skLineSegment(sketch, "E544", {"start": v(145.03, 55.28) * mm, "end": v(143.71, 55.14) * mm});
            skLineSegment(sketch, "E545", {"start": v(143.71, 55.14) * mm, "end": v(142.98, 54.05) * mm});
            skLineSegment(sketch, "E546", {"start": v(142.98, 54.05) * mm, "end": v(142.8, 52.77) * mm});
            skLineSegment(sketch, "E547", {"start": v(142.8, 52.77) * mm, "end": v(142.2, 51.4) * mm});
            skLineSegment(sketch, "E548", {"start": v(142.2, 51.4) * mm, "end": v(140.98, 50.63) * mm});
            skLineSegment(sketch, "E549", {"start": v(140.98, 50.63) * mm, "end": v(139.98, 50.62) * mm});
            skLineSegment(sketch, "E550", {"start": v(115.29, 50.82) * mm, "end": v(115.29, 27.64) * mm});
            skLineSegment(sketch, "E551", {"start": v(115.29, 27.64) * mm, "end": v(330.2, 35.66) * mm});
            skLineSegment(sketch, "E552", {"start": v(330.2, 35.66) * mm, "end": v(330.2, 77.35) * mm});
            skLineSegment(sketch, "E553", {"start": v(330.2, 77.35) * mm, "end": v(326.26, 76.89) * mm});
            skLineSegment(sketch, "E554", {"start": v(326.26, 76.89) * mm, "end": v(323.74, 74.02) * mm});
            skLineSegment(sketch, "E555", {"start": v(323.74, 74.02) * mm, "end": v(322.59, 77.23) * mm});
            skLineSegment(sketch, "E556", {"start": v(322.59, 77.23) * mm, "end": v(321.21, 80.9) * mm});
            skLineSegment(sketch, "E557", {"start": v(321.21, 80.9) * mm, "end": v(319.95, 77) * mm});
            skLineSegment(sketch, "E558", {"start": v(319.95, 77) * mm, "end": v(319.14, 73.67) * mm});
            skLineSegment(sketch, "E559", {"start": v(319.14, 73.67) * mm, "end": v(318.1, 76.31) * mm});
            skLineSegment(sketch, "E560", {"start": v(318.1, 76.31) * mm, "end": v(317.88, 81.02) * mm});
            skLineSegment(sketch, "E561", {"start": v(317.88, 81.02) * mm, "end": v(316.04, 75.5) * mm});
            skLineSegment(sketch, "E562", {"start": v(316.04, 75.5) * mm, "end": v(315.58, 73.67) * mm});
            skLineSegment(sketch, "E563", {"start": v(315.58, 73.67) * mm, "end": v(313.29, 74.13) * mm});
            skLineSegment(sketch, "E564", {"start": v(313.29, 74.13) * mm, "end": v(313.29, 76.89) * mm});
            skLineSegment(sketch, "E565", {"start": v(313.29, 76.89) * mm, "end": v(311.1, 76.31) * mm});
            skLineSegment(sketch, "E566", {"start": v(311.1, 76.31) * mm, "end": v(310.65, 72.87) * mm});
            skLineSegment(sketch, "E567", {"start": v(310.65, 72.87) * mm, "end": v(310.53, 69.3) * mm});
            skLineSegment(sketch, "E568", {"start": v(310.53, 69.3) * mm, "end": v(307.54, 73.1) * mm});
            skLineSegment(sketch, "E569", {"start": v(307.54, 73.1) * mm, "end": v(306.4, 70.68) * mm});
            skLineSegment(sketch, "E570", {"start": v(306.4, 70.68) * mm, "end": v(305.02, 75.97) * mm});
            skLineSegment(sketch, "E571", {"start": v(305.02, 75.97) * mm, "end": v(303.76, 73.1) * mm});
            skLineSegment(sketch, "E572", {"start": v(303.76, 73.1) * mm, "end": v(302.5, 75.74) * mm});
            skLineSegment(sketch, "E573", {"start": v(302.5, 75.74) * mm, "end": v(300.43, 68.04) * mm});
            skLineSegment(sketch, "E574", {"start": v(300.43, 68.04) * mm, "end": v(298.93, 65.4) * mm});
            skLineSegment(sketch, "E575", {"start": v(298.93, 65.4) * mm, "end": v(297.9, 60.8) * mm});
            skLineSegment(sketch, "E576", {"start": v(297.9, 60.8) * mm, "end": v(295.49, 59.82) * mm});
            skLineSegment(sketch, "E577", {"start": v(284.52, 65.62) * mm, "end": v(282.63, 66.08) * mm});
            skLineSegment(sketch, "E578", {"start": v(275.5, 61.26) * mm, "end": v(272.08, 56.52) * mm});
            skLineSegment(sketch, "E579", {"start": v(261.34, 58.36) * mm, "end": v(260.37, 57.51) * mm});
            skLineSegment(sketch, "E580", {"start": v(260.37, 57.51) * mm, "end": v(259.47, 59.53) * mm});
            skLineSegment(sketch, "E581", {"start": v(259.47, 59.53) * mm, "end": v(259.26, 63.22) * mm});
            skLineSegment(sketch, "E582", {"start": v(259.26, 63.22) * mm, "end": v(258.03, 64.52) * mm});
            skLineSegment(sketch, "E583", {"start": v(258.03, 64.52) * mm, "end": v(256.87, 63.44) * mm});
            skLineSegment(sketch, "E584", {"start": v(256.87, 63.44) * mm, "end": v(256.58, 59.17) * mm});
            skLineSegment(sketch, "E585", {"start": v(256.58, 59.17) * mm, "end": v(254.92, 66.33) * mm});
            skLineSegment(sketch, "E586", {"start": v(254.92, 66.33) * mm, "end": v(254.12, 66.48) * mm});
            skLineSegment(sketch, "E587", {"start": v(254.12, 66.48) * mm, "end": v(253.25, 65.25) * mm});
            skLineSegment(sketch, "E588", {"start": v(253.25, 65.25) * mm, "end": v(251.59, 60.76) * mm});
            skLineSegment(sketch, "E589", {"start": v(251.59, 60.76) * mm, "end": v(250.43, 60.47) * mm});
            skLineSegment(sketch, "E590", {"start": v(250.43, 60.47) * mm, "end": v(246.74, 61.78) * mm});
            skLineSegment(sketch, "E591", {"start": v(246.74, 61.78) * mm, "end": v(245.87, 62.2) * mm});
            skLineSegment(sketch, "E592", {"start": v(245.87, 62.2) * mm, "end": v(245.58, 66.4) * mm});
            skLineSegment(sketch, "E593", {"start": v(245.58, 66.4) * mm, "end": v(244.28, 63.22) * mm});
            skLineSegment(sketch, "E594", {"start": v(244.28, 63.22) * mm, "end": v(242.55, 65.75) * mm});
            skLineSegment(sketch, "E595", {"start": v(242.55, 65.75) * mm, "end": v(241.6, 64.02) * mm});
            skLineSegment(sketch, "E596", {"start": v(241.6, 64.02) * mm, "end": v(240.38, 61.56) * mm});
            skLineSegment(sketch, "E597", {"start": v(240.38, 61.56) * mm, "end": v(237.55, 62.35) * mm});
            skLineSegment(sketch, "E598", {"start": v(237.55, 62.35) * mm, "end": v(233.09, 63.62) * mm});
            skLineSegment(sketch, "E599", {"start": v(222.58, 63.33) * mm, "end": v(220.38, 62.07) * mm});
            skLineSegment(sketch, "E600", {"start": v(251, 64.56) * mm, "end": v(250.09, 64.62) * mm});
            skSolve(sketch);
        }
        {
            var Q0;
            {var subQ4=sQuery(id+"F0.wireOp",EDGE,"E344");Q0=makeQuery(id+"F0.imprint","IMPRINT",FACE,{"disambiguationData":[TD([[makeQuery(id+"F0.imprint","IMPRINT",EDGE,{"derivedFrom":subQ4}),-1.0]])]});}
            var Q1;
            {var subQ0=sQuery(id+"F0.wireOp",EDGE,"E409");Q1=makeQuery(id+"F0.imprint","IMPRINT",FACE,{"disambiguationData":[TD([[makeQuery(id+"F0.imprint","IMPRINT",EDGE,{"derivedFrom":subQ0}),1.0]])]});}
            var Q2;
            {var subQ7=sQuery(id+"F0.wireOp",EDGE,"E109");Q2=makeQuery(id+"F0.imprint","IMPRINT",FACE,{"disambiguationData":[TD([[makeQuery(id+"F0.imprint","IMPRINT",EDGE,{"derivedFrom":subQ7}),-1.0]])]});}
            var Q3;
            {var subQ0=sQuery(id+"F0.wireOp",EDGE,"E120");Q3=makeQuery(id+"F0.imprint","IMPRINT",FACE,{"disambiguationData":[TD([[makeQuery(id+"F0.imprint","IMPRINT",EDGE,{"derivedFrom":subQ0}),1.0]])]});}
            var Q4;
            Q4=makeQuery(id+"F0.imprint","IMPRINT",FACE,{"disambiguationData":[TD([[makeQuery(id+"F0.imprint","IMPRINT",EDGE,{"derivedFrom":sQuery(id+"F0.wireOp",EDGE,"E0")}),1.0]])]});
            extrude(context, id + "F1", {"entities" : qUnion([Q0, Q1, Q2, Q3, Q4]), "depth" : 3.17 * mm, "offsetDistance" : 25.4 * mm});
        }
    });
